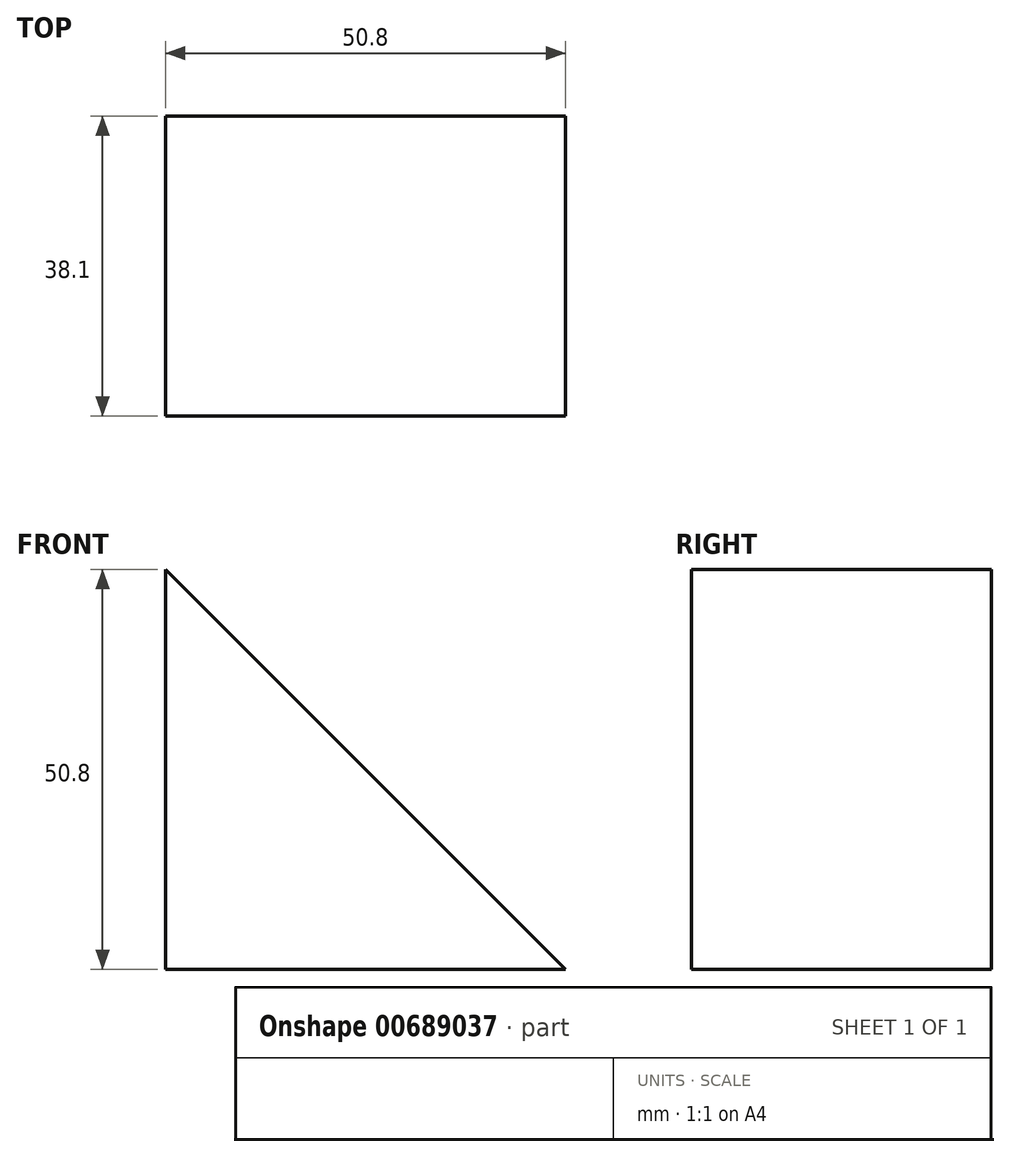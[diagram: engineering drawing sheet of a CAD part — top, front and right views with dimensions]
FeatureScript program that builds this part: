
annotation { "Feature Type Name" : "Feature", "Feature Type Description" : "" }
export const myFeature = defineFeature(function(context is Context, id is Id, definition is map)
    precondition{}
    {
        {
            var Q0;
            Q0=qCreatedBy(makeId("Front.planeOp"),FACE);
            var sketch = newSketch(context, id + "F0", { "sketchPlane" : qUnion([Q0])});
            skLineSegment(sketch, "E0", {"start": v(0, 0) * mm, "end": v(-50.8, 0) * mm});
            skLineSegment(sketch, "E1", {"start": v(-50.8, 0) * mm, "end": v(-50.8, 50.8) * mm});
            skLineSegment(sketch, "E2", {"start": v(-50.8, 50.8) * mm, "end": v(0, 0) * mm});
            skSolve(sketch);
        }
        {
            var Q0;
            Q0=makeQuery(id+"F0.imprint","IMPRINT",FACE,{"disambiguationData":[TD([[makeQuery(id+"F0.imprint","IMPRINT",EDGE,{"derivedFrom":sQuery(id+"F0.wireOp",EDGE,"E0")}),-1.0]])]});
            extrude(context, id + "F1", {"entities" : qUnion([Q0]), "depth" : 38.1 * mm, "offsetDistance" : 25.4 * mm});
        }
    });
